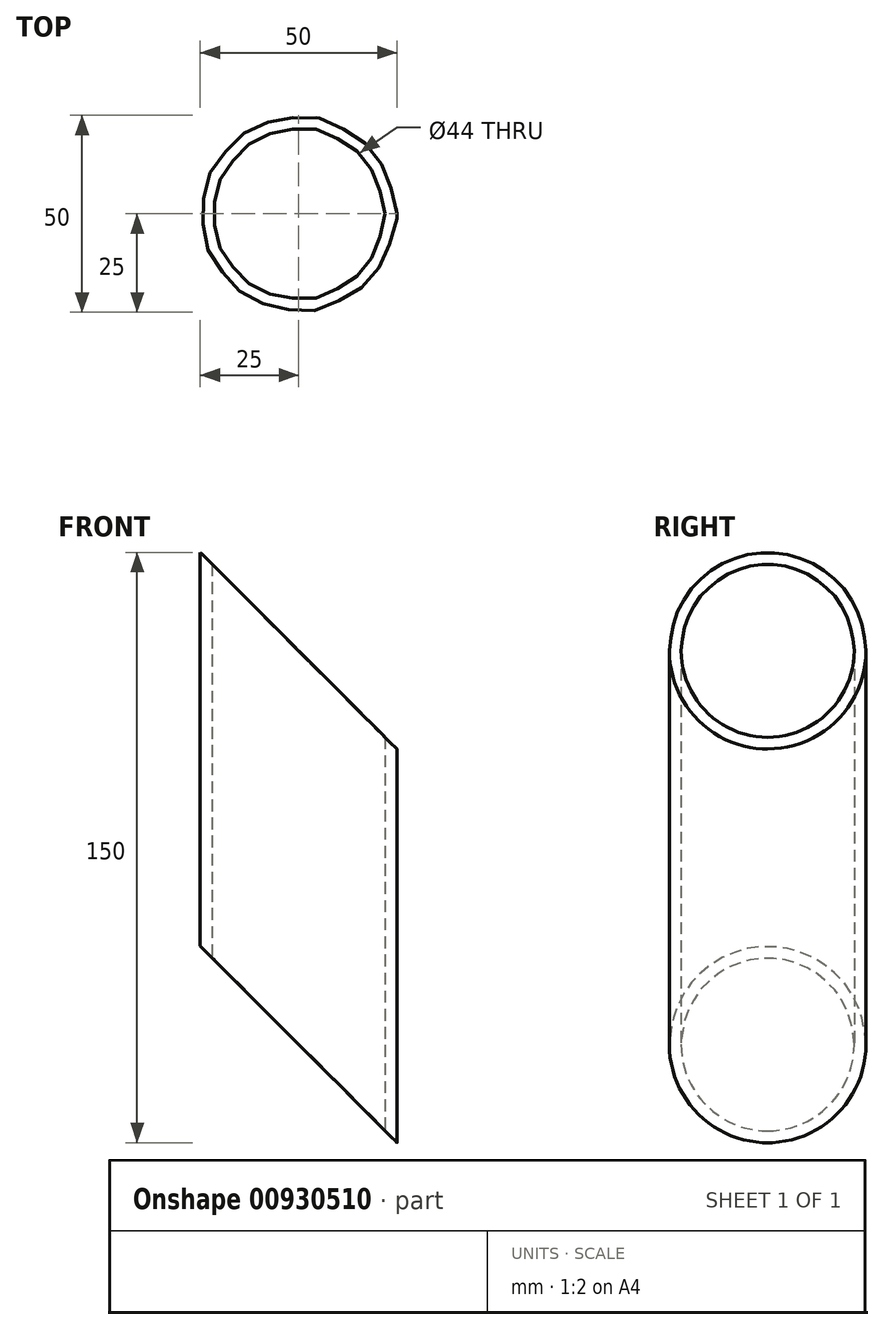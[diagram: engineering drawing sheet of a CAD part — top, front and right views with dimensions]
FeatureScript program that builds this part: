
annotation { "Feature Type Name" : "Feature", "Feature Type Description" : "" }
export const myFeature = defineFeature(function(context is Context, id is Id, definition is map)
    precondition{}
    {
        {
            var Q0;
            Q0=qCreatedBy(makeId("Top.planeOp"),FACE);
            var sketch = newSketch(context, id + "F0", { "sketchPlane" : qUnion([Q0])});
            skCircle(sketch, "E0", {"center": v(0, 0) * mm, "radius": 25 * mm});
            skCircle(sketch, "E1", {"center": v(0, 0) * mm, "radius": 22 * mm});
            skSolve(sketch);
        }
        {
            var Q0;
            Q0 = qSketchRegion(id + "F0", true);
            extrude(context, id + "F1", {"entities" : qUnion([Q0]), "depth" : 150 * mm, "offsetDistance" : 25 * mm});
        }
        {
            var Q0;
            Q0=qCreatedBy(makeId("Front.planeOp"),FACE);
            var sketch = newSketch(context, id + "F2", { "sketchPlane" : qUnion([Q0])});
            skLineSegment(sketch, "E2", {"start": v(-25, 150) * mm, "end": v(25, 100) * mm});
            skLineSegment(sketch, "E3", {"start": v(25, 100) * mm, "end": v(25, 150) * mm});
            skLineSegment(sketch, "E4", {"start": v(25, 150) * mm, "end": v(-25, 150) * mm});
            skSolve(sketch);
        }
        {
            var Q0;
            Q0=qCreatedBy(makeId("Front.planeOp"),FACE);
            var sketch = newSketch(context, id + "F3", { "sketchPlane" : qUnion([Q0])});
            skLineSegment(sketch, "E5", {"start": v(-25.03, 50) * mm, "end": v(-25.03, 0) * mm});
            skLineSegment(sketch, "E6", {"start": v(-25.03, 0) * mm, "end": v(24.97, 0) * mm});
            skLineSegment(sketch, "E7", {"start": v(24.97, 0) * mm, "end": v(-25.03, 50) * mm});
            skSolve(sketch);
        }
        {
            var Q0;
            Q0 = qSketchRegion(id + "F3", true);
            extrude(context, id + "F4", {"entities" : qUnion([Q0]), "operationType" : NewBodyOperationType.REMOVE, "endBound" : BoundingType.SYMMETRIC, "oppositeDirection" : true, "depth" : 60 * mm, "offsetDistance" : 25 * mm});
        }
        {
            var Q0;
            Q0 = qSketchRegion(id + "F2", true);
            extrude(context, id + "F5", {"entities" : qUnion([Q0]), "operationType" : NewBodyOperationType.REMOVE, "endBound" : BoundingType.SYMMETRIC, "oppositeDirection" : true, "depth" : 50 * mm, "offsetDistance" : 25 * mm});
        }
    });
